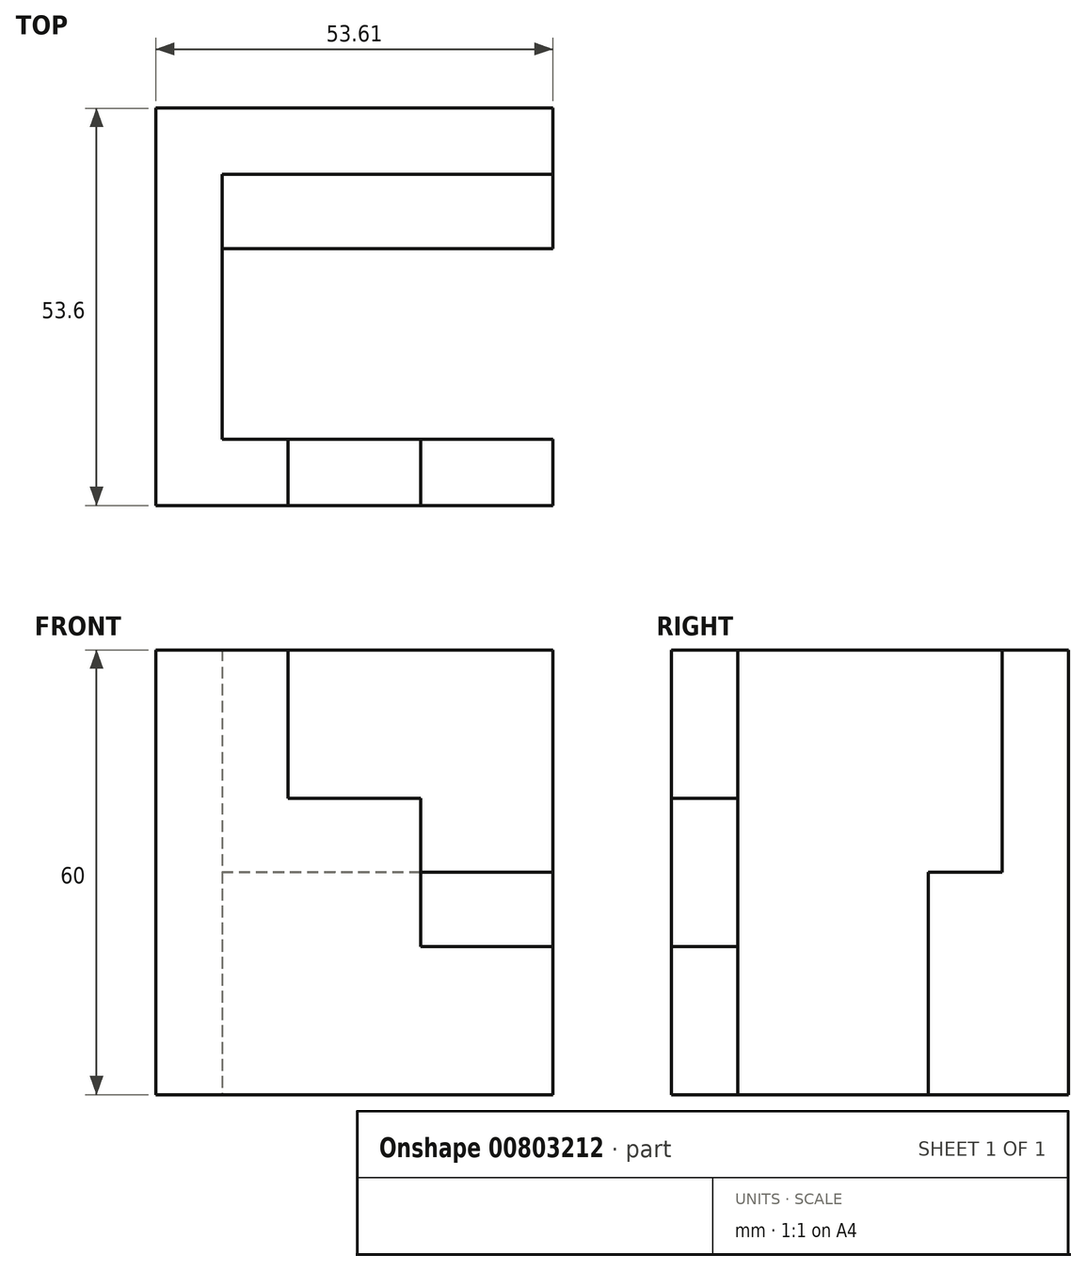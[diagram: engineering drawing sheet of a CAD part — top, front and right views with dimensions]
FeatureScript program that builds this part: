
annotation { "Feature Type Name" : "Feature", "Feature Type Description" : "" }
export const myFeature = defineFeature(function(context is Context, id is Id, definition is map)
    precondition{}
    {
        {
            var Q0;
            Q0=qCreatedBy(makeId("Top.planeOp"),FACE);
            var sketch = newSketch(context, id + "F0", { "sketchPlane" : qUnion([Q0])});
            skLineSegment(sketch, "E0", {"start": v(-36.88, 8.93) * mm, "end": v(-36.88, -44.67) * mm});
            skLineSegment(sketch, "E1", {"start": v(-36.88, -44.67) * mm, "end": v(-19.01, -44.67) * mm});
            skLineSegment(sketch, "E2", {"start": v(-36.88, 8.93) * mm, "end": v(16.73, 8.93) * mm});
            skLineSegment(sketch, "E3", {"start": v(-19.01, -44.67) * mm, "end": v(-19.01, -35.74) * mm});
            skLineSegment(sketch, "E4", {"start": v(-19.01, -35.74) * mm, "end": v(-27.95, -35.74) * mm});
            skLineSegment(sketch, "E5", {"start": v(-27.95, -35.74) * mm, "end": v(-27.95, 0) * mm});
            skLineSegment(sketch, "E6", {"start": v(-27.95, 0) * mm, "end": v(16.73, 0) * mm});
            skLineSegment(sketch, "E7", {"start": v(16.73, 0) * mm, "end": v(16.73, 8.93) * mm});
            skLineSegment(sketch, "E8", {"start": v(-19.01, -35.74) * mm, "end": v(-1.14, -35.74) * mm});
            skLineSegment(sketch, "E9", {"start": v(-1.14, -35.74) * mm, "end": v(-1.14, -44.67) * mm});
            skLineSegment(sketch, "E10", {"start": v(-1.14, -44.67) * mm, "end": v(-19.01, -44.67) * mm});
            skLineSegment(sketch, "E11", {"start": v(-1.14, -35.74) * mm, "end": v(16.73, -35.74) * mm});
            skLineSegment(sketch, "E12", {"start": v(16.73, -35.74) * mm, "end": v(16.73, -44.67) * mm});
            skLineSegment(sketch, "E13", {"start": v(16.73, -44.67) * mm, "end": v(-1.14, -44.67) * mm});
            skLineSegment(sketch, "E14", {"start": v(16.73, 0) * mm, "end": v(16.73, -10) * mm});
            skLineSegment(sketch, "E15", {"start": v(16.73, -10) * mm, "end": v(-27.95, -10) * mm});
            skLineSegment(sketch, "E16", {"start": v(-27.95, -10) * mm, "end": v(-27.95, 0) * mm});
            skSolve(sketch);
        }
        {
            var Q0;
            Q0=makeQuery(id+"F0.imprint","IMPRINT",FACE,{"disambiguationData":[TD([[makeQuery(id+"F0.imprint","IMPRINT",EDGE,{"derivedFrom":sQuery(id+"F0.wireOp",EDGE,"E0")}),1.0]])]});
            extrude(context, id + "F1", {"entities" : qUnion([Q0]), "depth" : 60 * mm, "offsetDistance" : 25 * mm});
        }
        {
            var Q0;
            Q0=makeQuery(id+"F0.imprint","IMPRINT",FACE,{"disambiguationData":[TD([[makeQuery(id+"F0.imprint","IMPRINT",EDGE,{"derivedFrom":sQuery(id+"F0.wireOp",EDGE,"E6")}),-1.0]])]});
            extrude(context, id + "F2", {"entities" : qUnion([Q0]), "operationType" : NewBodyOperationType.ADD, "depth" : 30 * mm, "offsetDistance" : 25 * mm});
        }
        {
            var Q0;
            Q0=makeQuery(id+"F0.imprint","IMPRINT",FACE,{"disambiguationData":[TD([[makeQuery(id+"F0.imprint","IMPRINT",EDGE,{"derivedFrom":sQuery(id+"F0.wireOp",EDGE,"E3")}),-1.0]])]});
            extrude(context, id + "F3", {"entities" : qUnion([Q0]), "operationType" : NewBodyOperationType.ADD, "depth" : 40 * mm, "offsetDistance" : 25 * mm});
        }
        {
            var Q0;
            Q0=makeQuery(id+"F0.imprint","IMPRINT",FACE,{"disambiguationData":[TD([[makeQuery(id+"F0.imprint","IMPRINT",EDGE,{"derivedFrom":sQuery(id+"F0.wireOp",EDGE,"E9")}),1.0]])]});
            extrude(context, id + "F4", {"entities" : qUnion([Q0]), "operationType" : NewBodyOperationType.ADD, "depth" : 20 * mm, "offsetDistance" : 25 * mm});
        }
    });
